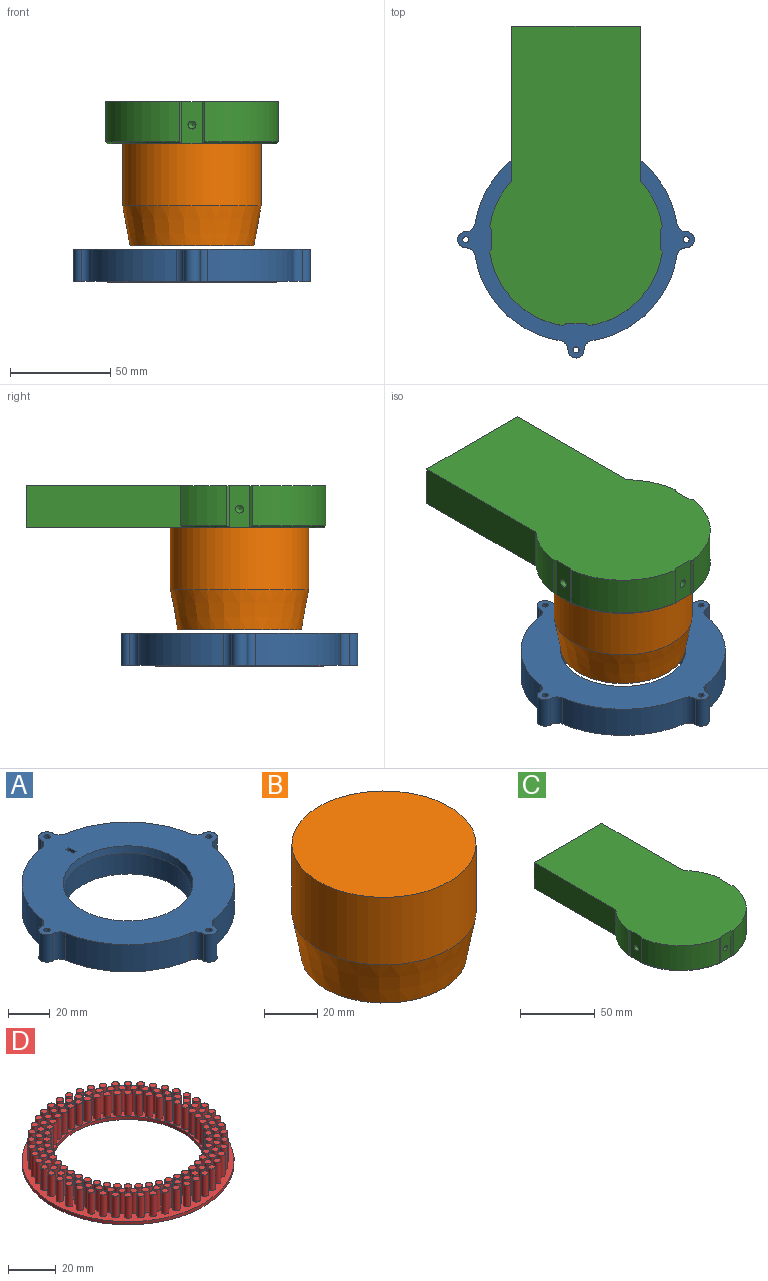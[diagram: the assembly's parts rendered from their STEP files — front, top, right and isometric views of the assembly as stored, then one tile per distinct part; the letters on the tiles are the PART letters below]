
ASSEMBLY  parts=4 mates=3
PART A: 36 faces, bbox 118x118x16 mm
  f0: cylinder r=45mm len=90mm, axis (0,0,1), area 3392.9mm2, adj f5,f22
  f1: cylinder r=1.5mm len=16mm, axis (0,0,-1), area 150.8mm2, adj f5,f35
  f2: cylinder r=1.5mm len=16mm, axis (0,0,-1), area 150.8mm2, adj f5,f35
  f3: cylinder r=1.5mm len=16mm, axis (0,0,-1), area 150.8mm2, adj f5,f35
  f4: cylinder r=1.5mm len=16mm, axis (0,0,-1), area 150.8mm2, adj f5,f35
  f5: plane 118x118mm, normal (0,0,-1), area 2039mm2, adj f0,f1,f2,f3,f4,f6,f7,f8
  f6: cylinder r=4.68mm len=16mm, axis (0,0,-1), area 105.9mm2, adj f5,f8,f20,f35
  f7: cylinder r=4.68mm len=16mm, axis (0,0,-1), area 105.9mm2, adj f5,f8,f21,f35
  f8: cylinder r=4mm len=16mm, axis (0,0,-1), area 201.1mm2, adj f5,f6,f7,f35
  f9: cylinder r=4.68mm len=16mm, axis (0,0,-1), area 105.9mm2, adj f5,f11,f19,f35
  f10: cylinder r=4.68mm len=16mm, axis (0,0,-1), area 105.9mm2, adj f5,f11,f20,f35
  f11: cylinder r=4mm len=16mm, axis (0,0,-1), area 201.1mm2, adj f5,f9,f10,f35
  f12: cylinder r=4.68mm len=16mm, axis (0,0,-1), area 105.9mm2, adj f5,f14,f18,f35
  f13: cylinder r=4.68mm len=16mm, axis (0,0,-1), area 105.9mm2, adj f5,f14,f19,f35
  f14: cylinder r=4mm len=16mm, axis (0,0,-1), area 201.1mm2, adj f5,f12,f13,f35
  f15: cylinder r=4.68mm len=16mm, axis (0,0,-1), area 105.9mm2, adj f5,f16,f18,f35
  f16: cylinder r=4mm len=16mm, axis (0,0,-1), area 201.1mm2, adj f5,f15,f17,f35
  f17: cylinder r=4.68mm len=16mm, axis (0,0,-1), area 105.9mm2, adj f5,f16,f21,f35
  f18: cylinder r=51mm len=42.43mm, axis (0,0,1), area 1026.3mm2, adj f5,f12,f15,f35
  f19: cylinder r=51mm len=42.43mm, axis (0,0,1), area 1026.3mm2, adj f5,f9,f13,f35
  f20: cylinder r=51mm len=42.43mm, axis (0,0,1), area 1026.3mm2, adj f5,f6,f10,f35
  f21: cylinder r=51mm len=42.43mm, axis (0,0,1), area 1026.3mm2, adj f5,f7,f17,f35
  f22: plane 90x90mm, normal (0,0,-1), area 279.6mm2, adj f0,f24
  f23: plane 67x67mm, normal (0,0,-1), area 408.4mm2, adj f25,f31
  f24: cylinder r=44mm len=88mm, axis (0,0,-1), area 552.9mm2, adj f22,f26
  f25: cylinder r=33.5mm len=67mm, axis (0,0,-1), area 421mm2, adj f23,f26
  f26: plane 88x88mm, normal (0,0,-1), area 2546.5mm2, adj f24,f25,f27,f28,f29,f30
  f27: plane 5x2mm, normal (1,0,0), area 10mm2, adj f26,f28,f30,f35
  f28: plane 2x2mm, normal (0,1,0), area 4mm2, adj f26,f27,f29,f35
  f29: plane 5x2mm, normal (-1,0,0), area 10mm2, adj f26,f28,f30,f35
  f30: plane 2x2mm, normal (0,-1,0), area 4mm2, adj f26,f27,f29,f35
  f31: cylinder r=31.5mm len=63mm, axis (0,0,1), area 2375mm2, adj f23,f32
  f32: plane 63x63mm, normal (0,0,-1), area 194.8mm2, adj f31,f33
  f33: cylinder r=30.5mm len=61mm, axis (0,0,1), area 2299.6mm2, adj f32,f34
  f34: cone r=31.92mm half-angle=10.2deg, axis (0,0,1), area 788.1mm2, adj f33,f35
  f35: plane 118x118mm, normal (0,0,1), area 5328.6mm2, adj f1,f2,f3,f4,f6,f7,f8,f9
PART B: 4 faces, bbox 69x69x51 mm
  f0: cylinder r=34.5mm len=69mm, axis (0,0,1), area 6719.9mm2, adj f1,f3
  f1: plane 69x69mm, normal (0,0,1), area 3739.3mm2, adj f0
  f2: plane 61.8x61.8mm, normal (0,0,-1), area 2999.6mm2, adj f3
  f3: cone r=34.5mm half-angle=10.2deg, axis (0,0,1), area 4175.2mm2, adj f0,f2
PART C: 28 faces, bbox 86.4x149.7x21 mm
  f0: plane 21.02x1.32mm, normal (-0.83,0.56,0), area 32.3mm2, adj f1,f15,f16,f17,f27
  f1: cylinder r=43.5mm len=36.68mm, axis (0,0,-1), area 1111.7mm2, adj f0,f2,f16,f27
  f2: plane 21.02x1.32mm, normal (0.56,-0.83,0), area 32.3mm2, adj f1,f3,f16,f17,f27
  f3: plane 21x10.1mm, normal (0,-1,0), area 199.5mm2, adj f2,f4,f16,f17,f23
  f4: plane 21.02x1.32mm, normal (-0.56,-0.83,0), area 32.3mm2, adj f3,f5,f16,f17,f26
  f5: cylinder r=43.5mm len=36.68mm, axis (0,0,-1), area 1111.7mm2, adj f4,f6,f16,f26
  f6: plane 21.02x1.32mm, normal (0.83,0.56,0), area 32.3mm2, adj f5,f7,f16,f17,f26
  f7: plane 21x10.1mm, normal (1,0,0), area 199.5mm2, adj f6,f8,f16,f17,f21
  f8: plane 21.02x1.32mm, normal (0.83,-0.56,0), area 32.3mm2, adj f7,f9,f16,f17,f24
  f9: cylinder r=43.5mm len=23.12mm, axis (0,0,-1), area 520mm2, adj f8,f10,f16,f24
  f10: plane 78.51x21.02mm, normal (1,0,0), area 1617.7mm2, adj f9,f11,f16,f17,f24
  f11: plane 64x21mm, normal (0,1,0), area 1344mm2, adj f10,f12,f16,f17
  f12: plane 78.51x21.02mm, normal (-1,0,0), area 1617.7mm2, adj f11,f13,f16,f17,f25
  f13: cylinder r=43.5mm len=23.12mm, axis (0,0,-1), area 520mm2, adj f12,f14,f16,f25
  f14: plane 21.02x1.32mm, normal (-0.83,-0.56,0), area 32.3mm2, adj f13,f15,f16,f17,f25
  f15: plane 21x10.1mm, normal (-1,0,0), area 199.5mm2, adj f0,f14,f16,f17,f19
  f16: plane 149.5x86.07mm, normal (0,0,1), area 10209.4mm2, adj f0,f1,f2,f3,f4,f5,f6,f7
  f17: plane 148.66x84.38mm, normal (0,0,-1), area 10045.9mm2, adj f0,f2,f3,f4,f6,f7,f8,f10
  f18: cone r=0mm half-angle=59deg, axis (-1,0,0), area 14.7mm2, adj f19
  f19: cylinder r=2mm len=5mm, axis (-1,0,0), area 62.8mm2, adj f15,f18
  f20: cone r=0mm half-angle=59deg, axis (1,0,0), area 14.7mm2, adj f21
  f21: cylinder r=2mm len=5mm, axis (1,0,0), area 62.8mm2, adj f7,f20
  f22: cone r=0mm half-angle=59deg, axis (0,-1,0), area 14.7mm2, adj f23
  f23: cylinder r=2mm len=5mm, axis (0,-1,0), area 62.8mm2, adj f3,f22
  f24: cone r=43.5mm half-angle=45deg, axis (0,0,1), area 36.3mm2, adj f8,f9,f10,f17
  f25: cone r=43.5mm half-angle=45deg, axis (0,0,1), area 36.3mm2, adj f12,f13,f14,f17
  f26: cone r=43.5mm half-angle=45deg, axis (0,0,1), area 79.3mm2, adj f4,f5,f6,f17
  f27: cone r=43.5mm half-angle=45deg, axis (0,0,1), area 79.3mm2, adj f0,f1,f2,f17
PART D: 292 faces, bbox 89x89x12.6 mm
  f0: cylinder r=32mm len=64mm, axis (0,0,-1), area 321.7mm2, adj f2,f3
  f1: cylinder r=44.5mm len=89mm, axis (0,0,-1), area 447.4mm2, adj f2,f3
  f2: plane 89x89mm, normal (0,0,1), area 1917.3mm2, adj f0,f1,f4,f6,f8,f10,f12,f14
  f3: plane 89x89mm, normal (0,0,-1), area 3004.1mm2, adj f0,f1
  f4: cylinder r=1.55mm len=11mm, axis (0,0,-1), area 107.1mm2, adj f2,f5
  f5: plane 3.1x3.1mm, normal (0,0,1), area 7.5mm2, adj f4
  f6: cylinder r=1.55mm len=11mm, axis (0,0,-1), area 107.1mm2, adj f2,f7
  f7: plane 3.1x3.1mm, normal (0,0,1), area 7.5mm2, adj f6
  f8: cylinder r=1.55mm len=11mm, axis (0,0,-1), area 107.1mm2, adj f2,f9
  f9: plane 3.1x3.1mm, normal (0,0,1), area 7.5mm2, adj f8
  f10: cylinder r=1.55mm len=11mm, axis (0,0,-1), area 107.1mm2, adj f2,f11
  f11: plane 3.1x3.1mm, normal (0,0,1), area 7.5mm2, adj f10
  f12: cylinder r=1.55mm len=11mm, axis (0,0,-1), area 107.1mm2, adj f2,f13
  f13: plane 3.1x3.1mm, normal (0,0,1), area 7.5mm2, adj f12
  f14: cylinder r=1.55mm len=11mm, axis (0,0,-1), area 107.1mm2, adj f2,f15
  f15: plane 3.1x3.1mm, normal (0,0,1), area 7.5mm2, adj f14
  f16: cylinder r=1.55mm len=11mm, axis (0,0,-1), area 107.1mm2, adj f2,f17
  f17: plane 3.1x3.1mm, normal (0,0,1), area 7.5mm2, adj f16
  f18: cylinder r=1.55mm len=11mm, axis (0,0,-1), area 107.1mm2, adj f2,f19
  f19: plane 3.1x3.1mm, normal (0,0,1), area 7.5mm2, adj f18
  f20: cylinder r=1.55mm len=11mm, axis (0,0,-1), area 107.1mm2, adj f2,f21
  f21: plane 3.1x3.1mm, normal (0,0,1), area 7.5mm2, adj f20
  f22: cylinder r=1.55mm len=11mm, axis (0,0,-1), area 107.1mm2, adj f2,f23
  f23: plane 3.1x3.1mm, normal (0,0,1), area 7.5mm2, adj f22
  f24: cylinder r=1.55mm len=11mm, axis (0,0,-1), area 107.1mm2, adj f2,f25
  f25: plane 3.1x3.1mm, normal (0,0,1), area 7.5mm2, adj f24
  f26: cylinder r=1.55mm len=11mm, axis (0,0,-1), area 107.1mm2, adj f2,f27
  f27: plane 3.1x3.1mm, normal (0,0,1), area 7.5mm2, adj f26
  f28: cylinder r=1.55mm len=11mm, axis (0,0,-1), area 107.1mm2, adj f2,f29
  f29: plane 3.1x3.1mm, normal (0,0,1), area 7.5mm2, adj f28
  f30: cylinder r=1.55mm len=11mm, axis (0,0,-1), area 107.1mm2, adj f2,f31
  f31: plane 3.1x3.1mm, normal (0,0,1), area 7.5mm2, adj f30
  f32: cylinder r=1.55mm len=11mm, axis (0,0,-1), area 107.1mm2, adj f2,f33
  f33: plane 3.1x3.1mm, normal (0,0,1), area 7.5mm2, adj f32
  f34: cylinder r=1.55mm len=11mm, axis (0,0,-1), area 107.1mm2, adj f2,f35
  f35: plane 3.1x3.1mm, normal (0,0,1), area 7.5mm2, adj f34
  f36: cylinder r=1.55mm len=11mm, axis (0,0,-1), area 107.1mm2, adj f2,f37
  f37: plane 3.1x3.1mm, normal (0,0,1), area 7.5mm2, adj f36
  f38: cylinder r=1.55mm len=11mm, axis (0,0,-1), area 107.1mm2, adj f2,f39
  f39: plane 3.1x3.1mm, normal (0,0,1), area 7.5mm2, adj f38
  f40: cylinder r=1.55mm len=11mm, axis (0,0,-1), area 107.1mm2, adj f2,f41
  f41: plane 3.1x3.1mm, normal (0,0,1), area 7.5mm2, adj f40
  f42: cylinder r=1.55mm len=11mm, axis (0,0,-1), area 107.1mm2, adj f2,f43
  f43: plane 3.1x3.1mm, normal (0,0,1), area 7.5mm2, adj f42
  f44: cylinder r=1.55mm len=11mm, axis (0,0,-1), area 107.1mm2, adj f2,f45
  f45: plane 3.1x3.1mm, normal (0,0,1), area 7.5mm2, adj f44
  f46: cylinder r=1.55mm len=11mm, axis (0,0,-1), area 107.1mm2, adj f2,f47
  f47: plane 3.1x3.1mm, normal (0,0,1), area 7.5mm2, adj f46
  f48: cylinder r=1.55mm len=11mm, axis (0,0,-1), area 107.1mm2, adj f2,f49
  f49: plane 3.1x3.1mm, normal (0,0,1), area 7.5mm2, adj f48
  f50: cylinder r=1.55mm len=11mm, axis (0,0,-1), area 107.1mm2, adj f2,f51
  f51: plane 3.1x3.1mm, normal (0,0,1), area 7.5mm2, adj f50
  f52: cylinder r=1.55mm len=11mm, axis (0,0,-1), area 107.1mm2, adj f2,f53
  f53: plane 3.1x3.1mm, normal (0,0,1), area 7.5mm2, adj f52
  f54: cylinder r=1.55mm len=11mm, axis (0,0,-1), area 107.1mm2, adj f2,f55
  f55: plane 3.1x3.1mm, normal (0,0,1), area 7.5mm2, adj f54
  f56: cylinder r=1.55mm len=11mm, axis (0,0,-1), area 107.1mm2, adj f2,f57
  f57: plane 3.1x3.1mm, normal (0,0,1), area 7.5mm2, adj f56
  f58: cylinder r=1.55mm len=11mm, axis (0,0,-1), area 107.1mm2, adj f2,f59
  f59: plane 3.1x3.1mm, normal (0,0,1), area 7.5mm2, adj f58
  f60: cylinder r=1.55mm len=11mm, axis (0,0,-1), area 107.1mm2, adj f2,f61
  f61: plane 3.1x3.1mm, normal (0,0,1), area 7.5mm2, adj f60
  f62: cylinder r=1.55mm len=11mm, axis (0,0,-1), area 107.1mm2, adj f2,f63
  f63: plane 3.1x3.1mm, normal (0,0,1), area 7.5mm2, adj f62
  f64: cylinder r=1.55mm len=11mm, axis (0,0,-1), area 107.1mm2, adj f2,f65
  f65: plane 3.1x3.1mm, normal (0,0,1), area 7.5mm2, adj f64
  f66: cylinder r=1.55mm len=11mm, axis (0,0,-1), area 107.1mm2, adj f2,f67
  f67: plane 3.1x3.1mm, normal (0,0,1), area 7.5mm2, adj f66
  f68: cylinder r=1.55mm len=11mm, axis (0,0,-1), area 107.1mm2, adj f2,f69
  f69: plane 3.1x3.1mm, normal (0,0,1), area 7.5mm2, adj f68
  f70: cylinder r=1.55mm len=11mm, axis (0,0,-1), area 107.1mm2, adj f2,f71
  f71: plane 3.1x3.1mm, normal (0,0,1), area 7.5mm2, adj f70
  f72: cylinder r=1.55mm len=11mm, axis (0,0,-1), area 107.1mm2, adj f2,f73
  f73: plane 3.1x3.1mm, normal (0,0,1), area 7.5mm2, adj f72
  f74: cylinder r=1.55mm len=11mm, axis (0,0,-1), area 107.1mm2, adj f2,f75
  f75: plane 3.1x3.1mm, normal (0,0,1), area 7.5mm2, adj f74
  f76: cylinder r=1.55mm len=11mm, axis (0,0,-1), area 107.1mm2, adj f2,f77
  f77: plane 3.1x3.1mm, normal (0,0,1), area 7.5mm2, adj f76
  f78: cylinder r=1.55mm len=11mm, axis (0,0,-1), area 107.1mm2, adj f2,f79
  f79: plane 3.1x3.1mm, normal (0,0,1), area 7.5mm2, adj f78
  f80: cylinder r=1.55mm len=11mm, axis (0,0,-1), area 107.1mm2, adj f2,f81
  f81: plane 3.1x3.1mm, normal (0,0,1), area 7.5mm2, adj f80
  f82: cylinder r=1.55mm len=11mm, axis (0,0,-1), area 107.1mm2, adj f2,f83
  f83: plane 3.1x3.1mm, normal (0,0,1), area 7.5mm2, adj f82
  f84: cylinder r=1.55mm len=11mm, axis (0,0,-1), area 107.1mm2, adj f2,f85
  f85: plane 3.1x3.1mm, normal (0,0,1), area 7.5mm2, adj f84
  f86: cylinder r=1.55mm len=11mm, axis (0,0,-1), area 107.1mm2, adj f2,f87
  f87: plane 3.1x3.1mm, normal (0,0,1), area 7.5mm2, adj f86
  f88: cylinder r=1.55mm len=11mm, axis (0,0,-1), area 107.1mm2, adj f2,f89
  f89: plane 3.1x3.1mm, normal (0,0,1), area 7.5mm2, adj f88
  f90: cylinder r=1.55mm len=11mm, axis (0,0,-1), area 107.1mm2, adj f2,f91
  f91: plane 3.1x3.1mm, normal (0,0,1), area 7.5mm2, adj f90
  f92: cylinder r=1.55mm len=11mm, axis (0,0,-1), area 107.1mm2, adj f2,f93
  f93: plane 3.1x3.1mm, normal (0,0,1), area 7.5mm2, adj f92
  f94: cylinder r=1.55mm len=11mm, axis (0,0,-1), area 107.1mm2, adj f2,f95
  f95: plane 3.1x3.1mm, normal (0,0,1), area 7.5mm2, adj f94
  f96: cylinder r=1.55mm len=11mm, axis (0,0,-1), area 107.1mm2, adj f2,f97
  f97: plane 3.1x3.1mm, normal (0,0,1), area 7.5mm2, adj f96
  f98: cylinder r=1.55mm len=11mm, axis (0,0,-1), area 107.1mm2, adj f2,f99
  f99: plane 3.1x3.1mm, normal (0,0,1), area 7.5mm2, adj f98
  f100: cylinder r=1.55mm len=11mm, axis (0,0,-1), area 107.1mm2, adj f2,f101
  f101: plane 3.1x3.1mm, normal (0,0,1), area 7.5mm2, adj f100
  f102: cylinder r=1.55mm len=11mm, axis (0,0,-1), area 107.1mm2, adj f2,f103
  f103: plane 3.1x3.1mm, normal (0,0,1), area 7.5mm2, adj f102
  f104: cylinder r=1.55mm len=11mm, axis (0,0,-1), area 107.1mm2, adj f2,f105
  f105: plane 3.1x3.1mm, normal (0,0,1), area 7.5mm2, adj f104
  f106: cylinder r=1.55mm len=11mm, axis (0,0,-1), area 107.1mm2, adj f2,f107
  f107: plane 3.1x3.1mm, normal (0,0,1), area 7.5mm2, adj f106
  f108: cylinder r=1.55mm len=11mm, axis (0,0,-1), area 107.1mm2, adj f2,f109
  f109: plane 3.1x3.1mm, normal (0,0,1), area 7.5mm2, adj f108
  f110: cylinder r=1.55mm len=11mm, axis (0,0,-1), area 107.1mm2, adj f2,f111
  f111: plane 3.1x3.1mm, normal (0,0,1), area 7.5mm2, adj f110
  f112: cylinder r=1.55mm len=11mm, axis (0,0,-1), area 107.1mm2, adj f2,f113
  f113: plane 3.1x3.1mm, normal (0,0,1), area 7.5mm2, adj f112
  f114: cylinder r=1.55mm len=11mm, axis (0,0,-1), area 107.1mm2, adj f2,f115
  f115: plane 3.1x3.1mm, normal (0,0,1), area 7.5mm2, adj f114
  f116: cylinder r=1.55mm len=11mm, axis (0,0,-1), area 107.1mm2, adj f2,f117
  f117: plane 3.1x3.1mm, normal (0,0,1), area 7.5mm2, adj f116
  f118: cylinder r=1.55mm len=11mm, axis (0,0,-1), area 107.1mm2, adj f2,f119
  f119: plane 3.1x3.1mm, normal (0,0,1), area 7.5mm2, adj f118
  f120: cylinder r=1.55mm len=11mm, axis (0,0,-1), area 107.1mm2, adj f2,f121
  f121: plane 3.1x3.1mm, normal (0,0,1), area 7.5mm2, adj f120
  f122: cylinder r=1.55mm len=11mm, axis (0,0,-1), area 107.1mm2, adj f2,f123
  f123: plane 3.1x3.1mm, normal (0,0,1), area 7.5mm2, adj f122
  f124: cylinder r=1.55mm len=11mm, axis (0,0,-1), area 107.1mm2, adj f2,f125
  f125: plane 3.1x3.1mm, normal (0,0,1), area 7.5mm2, adj f124
  f126: cylinder r=1.55mm len=11mm, axis (0,0,-1), area 107.1mm2, adj f2,f127
  f127: plane 3.1x3.1mm, normal (0,0,1), area 7.5mm2, adj f126
  f128: cylinder r=1.55mm len=11mm, axis (0,0,-1), area 107.1mm2, adj f2,f129
  f129: plane 3.1x3.1mm, normal (0,0,1), area 7.5mm2, adj f128
  f130: cylinder r=1.55mm len=11mm, axis (0,0,-1), area 107.1mm2, adj f2,f131
  f131: plane 3.1x3.1mm, normal (0,0,1), area 7.5mm2, adj f130
  f132: cylinder r=1.55mm len=11mm, axis (0,0,-1), area 107.1mm2, adj f2,f133
  f133: plane 3.1x3.1mm, normal (0,0,1), area 7.5mm2, adj f132
  f134: cylinder r=1.55mm len=11mm, axis (0,0,-1), area 107.1mm2, adj f2,f135
  f135: plane 3.1x3.1mm, normal (0,0,1), area 7.5mm2, adj f134
  f136: cylinder r=1.55mm len=11mm, axis (0,0,-1), area 107.1mm2, adj f2,f137
  f137: plane 3.1x3.1mm, normal (0,0,1), area 7.5mm2, adj f136
  f138: cylinder r=1.55mm len=11mm, axis (0,0,-1), area 107.1mm2, adj f2,f139
  f139: plane 3.1x3.1mm, normal (0,0,1), area 7.5mm2, adj f138
  f140: cylinder r=1.55mm len=11mm, axis (0,0,-1), area 107.1mm2, adj f2,f141
  f141: plane 3.1x3.1mm, normal (0,0,1), area 7.5mm2, adj f140
  f142: cylinder r=1.55mm len=11mm, axis (0,0,-1), area 107.1mm2, adj f2,f143
  f143: plane 3.1x3.1mm, normal (0,0,1), area 7.5mm2, adj f142
  f144: cylinder r=1.55mm len=11mm, axis (0,0,-1), area 107.1mm2, adj f2,f145
  f145: plane 3.1x3.1mm, normal (0,0,1), area 7.5mm2, adj f144
  f146: cylinder r=1.55mm len=11mm, axis (0,0,-1), area 107.1mm2, adj f2,f147
  f147: plane 3.1x3.1mm, normal (0,0,1), area 7.5mm2, adj f146
  f148: cylinder r=1.55mm len=11mm, axis (0,0,-1), area 107.1mm2, adj f2,f149
  f149: plane 3.1x3.1mm, normal (0,0,1), area 7.5mm2, adj f148
  f150: cylinder r=1.55mm len=11mm, axis (0,0,-1), area 107.1mm2, adj f2,f151
  f151: plane 3.1x3.1mm, normal (0,0,1), area 7.5mm2, adj f150
  f152: cylinder r=1.55mm len=11mm, axis (0,0,-1), area 107.1mm2, adj f2,f153
  f153: plane 3.1x3.1mm, normal (0,0,1), area 7.5mm2, adj f152
  f154: cylinder r=1.55mm len=11mm, axis (0,0,-1), area 107.1mm2, adj f2,f155
  f155: plane 3.1x3.1mm, normal (0,0,1), area 7.5mm2, adj f154
  f156: cylinder r=1.55mm len=11mm, axis (0,0,-1), area 107.1mm2, adj f2,f157
  f157: plane 3.1x3.1mm, normal (0,0,1), area 7.5mm2, adj f156
  f158: cylinder r=1.55mm len=11mm, axis (0,0,-1), area 107.1mm2, adj f2,f159
  f159: plane 3.1x3.1mm, normal (0,0,1), area 7.5mm2, adj f158
  f160: cylinder r=1.55mm len=11mm, axis (0,0,-1), area 107.1mm2, adj f2,f161
  f161: plane 3.1x3.1mm, normal (0,0,1), area 7.5mm2, adj f160
  f162: cylinder r=1.55mm len=11mm, axis (0,0,-1), area 107.1mm2, adj f2,f163
  f163: plane 3.1x3.1mm, normal (0,0,1), area 7.5mm2, adj f162
  f164: cylinder r=1.55mm len=11mm, axis (0,0,-1), area 107.1mm2, adj f2,f165
  f165: plane 3.1x3.1mm, normal (0,0,1), area 7.5mm2, adj f164
  f166: cylinder r=1.55mm len=11mm, axis (0,0,-1), area 107.1mm2, adj f2,f167
  f167: plane 3.1x3.1mm, normal (0,0,1), area 7.5mm2, adj f166
  f168: cylinder r=1.55mm len=11mm, axis (0,0,-1), area 107.1mm2, adj f2,f169
  f169: plane 3.1x3.1mm, normal (0,0,1), area 7.5mm2, adj f168
  f170: cylinder r=1.55mm len=11mm, axis (0,0,-1), area 107.1mm2, adj f2,f171
  f171: plane 3.1x3.1mm, normal (0,0,1), area 7.5mm2, adj f170
  f172: cylinder r=1.55mm len=11mm, axis (0,0,-1), area 107.1mm2, adj f2,f173
  f173: plane 3.1x3.1mm, normal (0,0,1), area 7.5mm2, adj f172
  f174: cylinder r=1.55mm len=11mm, axis (0,0,-1), area 107.1mm2, adj f2,f175
  f175: plane 3.1x3.1mm, normal (0,0,1), area 7.5mm2, adj f174
  f176: cylinder r=1.55mm len=11mm, axis (0,0,-1), area 107.1mm2, adj f2,f177
  f177: plane 3.1x3.1mm, normal (0,0,1), area 7.5mm2, adj f176
  f178: cylinder r=1.55mm len=11mm, axis (0,0,-1), area 107.1mm2, adj f2,f179
  f179: plane 3.1x3.1mm, normal (0,0,1), area 7.5mm2, adj f178
  f180: cylinder r=1.55mm len=11mm, axis (0,0,-1), area 107.1mm2, adj f2,f181
  f181: plane 3.1x3.1mm, normal (0,0,1), area 7.5mm2, adj f180
  f182: cylinder r=1.55mm len=11mm, axis (0,0,-1), area 107.1mm2, adj f2,f183
  f183: plane 3.1x3.1mm, normal (0,0,1), area 7.5mm2, adj f182
  f184: cylinder r=1.55mm len=11mm, axis (0,0,-1), area 107.1mm2, adj f2,f185
  f185: plane 3.1x3.1mm, normal (0,0,1), area 7.5mm2, adj f184
  f186: cylinder r=1.55mm len=11mm, axis (0,0,-1), area 107.1mm2, adj f2,f187
  f187: plane 3.1x3.1mm, normal (0,0,1), area 7.5mm2, adj f186
  f188: cylinder r=1.55mm len=11mm, axis (0,0,-1), area 107.1mm2, adj f2,f189
  f189: plane 3.1x3.1mm, normal (0,0,1), area 7.5mm2, adj f188
  f190: cylinder r=1.55mm len=11mm, axis (0,0,-1), area 107.1mm2, adj f2,f191
  f191: plane 3.1x3.1mm, normal (0,0,1), area 7.5mm2, adj f190
  f192: cylinder r=1.55mm len=11mm, axis (0,0,-1), area 107.1mm2, adj f2,f193
  f193: plane 3.1x3.1mm, normal (0,0,1), area 7.5mm2, adj f192
  f194: cylinder r=1.55mm len=11mm, axis (0,0,-1), area 107.1mm2, adj f2,f195
  f195: plane 3.1x3.1mm, normal (0,0,1), area 7.5mm2, adj f194
  f196: cylinder r=1.55mm len=11mm, axis (0,0,-1), area 107.1mm2, adj f2,f197
  f197: plane 3.1x3.1mm, normal (0,0,1), area 7.5mm2, adj f196
  f198: cylinder r=1.55mm len=11mm, axis (0,0,-1), area 107.1mm2, adj f2,f199
  f199: plane 3.1x3.1mm, normal (0,0,1), area 7.5mm2, adj f198
  f200: cylinder r=1.55mm len=11mm, axis (0,0,-1), area 107.1mm2, adj f2,f201
  f201: plane 3.1x3.1mm, normal (0,0,1), area 7.5mm2, adj f200
  f202: cylinder r=1.55mm len=11mm, axis (0,0,-1), area 107.1mm2, adj f2,f203
  f203: plane 3.1x3.1mm, normal (0,0,1), area 7.5mm2, adj f202
  f204: cylinder r=1.55mm len=11mm, axis (0,0,-1), area 107.1mm2, adj f2,f205
  f205: plane 3.1x3.1mm, normal (0,0,1), area 7.5mm2, adj f204
  f206: cylinder r=1.55mm len=11mm, axis (0,0,-1), area 107.1mm2, adj f2,f207
  f207: plane 3.1x3.1mm, normal (0,0,1), area 7.5mm2, adj f206
  f208: cylinder r=1.55mm len=11mm, axis (0,0,-1), area 107.1mm2, adj f2,f209
  f209: plane 3.1x3.1mm, normal (0,0,1), area 7.5mm2, adj f208
  f210: cylinder r=1.55mm len=11mm, axis (0,0,-1), area 107.1mm2, adj f2,f211
  f211: plane 3.1x3.1mm, normal (0,0,1), area 7.5mm2, adj f210
  f212: cylinder r=1.55mm len=11mm, axis (0,0,-1), area 107.1mm2, adj f2,f213
  f213: plane 3.1x3.1mm, normal (0,0,1), area 7.5mm2, adj f212
  f214: cylinder r=1.55mm len=11mm, axis (0,0,-1), area 107.1mm2, adj f2,f215
  f215: plane 3.1x3.1mm, normal (0,0,1), area 7.5mm2, adj f214
  f216: cylinder r=1.55mm len=11mm, axis (0,0,-1), area 107.1mm2, adj f2,f217
  f217: plane 3.1x3.1mm, normal (0,0,1), area 7.5mm2, adj f216
  f218: cylinder r=1.55mm len=11mm, axis (0,0,-1), area 107.1mm2, adj f2,f219
  f219: plane 3.1x3.1mm, normal (0,0,1), area 7.5mm2, adj f218
  f220: cylinder r=1.55mm len=11mm, axis (0,0,-1), area 107.1mm2, adj f2,f221
  f221: plane 3.1x3.1mm, normal (0,0,1), area 7.5mm2, adj f220
  f222: cylinder r=1.55mm len=11mm, axis (0,0,-1), area 107.1mm2, adj f2,f223
  f223: plane 3.1x3.1mm, normal (0,0,1), area 7.5mm2, adj f222
  f224: cylinder r=1.55mm len=11mm, axis (0,0,-1), area 107.1mm2, adj f2,f225
  f225: plane 3.1x3.1mm, normal (0,0,1), area 7.5mm2, adj f224
  f226: cylinder r=1.55mm len=11mm, axis (0,0,-1), area 107.1mm2, adj f2,f227
  f227: plane 3.1x3.1mm, normal (0,0,1), area 7.5mm2, adj f226
  f228: cylinder r=1.55mm len=11mm, axis (0,0,-1), area 107.1mm2, adj f2,f229
  f229: plane 3.1x3.1mm, normal (0,0,1), area 7.5mm2, adj f228
  f230: cylinder r=1.55mm len=11mm, axis (0,0,-1), area 107.1mm2, adj f2,f231
  f231: plane 3.1x3.1mm, normal (0,0,1), area 7.5mm2, adj f230
  f232: cylinder r=1.55mm len=11mm, axis (0,0,-1), area 107.1mm2, adj f2,f233
  f233: plane 3.1x3.1mm, normal (0,0,1), area 7.5mm2, adj f232
  f234: cylinder r=1.55mm len=11mm, axis (0,0,-1), area 107.1mm2, adj f2,f235
  f235: plane 3.1x3.1mm, normal (0,0,1), area 7.5mm2, adj f234
  f236: cylinder r=1.55mm len=11mm, axis (0,0,-1), area 107.1mm2, adj f2,f237
  f237: plane 3.1x3.1mm, normal (0,0,1), area 7.5mm2, adj f236
  f238: cylinder r=1.55mm len=11mm, axis (0,0,-1), area 107.1mm2, adj f2,f239
  f239: plane 3.1x3.1mm, normal (0,0,1), area 7.5mm2, adj f238
  f240: cylinder r=1.55mm len=11mm, axis (0,0,-1), area 107.1mm2, adj f2,f241
  f241: plane 3.1x3.1mm, normal (0,0,1), area 7.5mm2, adj f240
  f242: cylinder r=1.55mm len=11mm, axis (0,0,-1), area 107.1mm2, adj f2,f243
  f243: plane 3.1x3.1mm, normal (0,0,1), area 7.5mm2, adj f242
  f244: cylinder r=1.55mm len=11mm, axis (0,0,-1), area 107.1mm2, adj f2,f245
  f245: plane 3.1x3.1mm, normal (0,0,1), area 7.5mm2, adj f244
  f246: cylinder r=1.55mm len=11mm, axis (0,0,-1), area 107.1mm2, adj f2,f247
  f247: plane 3.1x3.1mm, normal (0,0,1), area 7.5mm2, adj f246
  f248: cylinder r=1.55mm len=11mm, axis (0,0,-1), area 107.1mm2, adj f2,f249
  f249: plane 3.1x3.1mm, normal (0,0,1), area 7.5mm2, adj f248
  f250: cylinder r=1.55mm len=11mm, axis (0,0,-1), area 107.1mm2, adj f2,f251
  f251: plane 3.1x3.1mm, normal (0,0,1), area 7.5mm2, adj f250
  f252: cylinder r=1.55mm len=11mm, axis (0,0,-1), area 107.1mm2, adj f2,f253
  f253: plane 3.1x3.1mm, normal (0,0,1), area 7.5mm2, adj f252
  f254: cylinder r=1.55mm len=11mm, axis (0,0,-1), area 107.1mm2, adj f2,f255
  f255: plane 3.1x3.1mm, normal (0,0,1), area 7.5mm2, adj f254
  f256: cylinder r=1.55mm len=11mm, axis (0,0,-1), area 107.1mm2, adj f2,f257
  f257: plane 3.1x3.1mm, normal (0,0,1), area 7.5mm2, adj f256
  f258: cylinder r=1.55mm len=11mm, axis (0,0,-1), area 107.1mm2, adj f2,f259
  f259: plane 3.1x3.1mm, normal (0,0,1), area 7.5mm2, adj f258
  f260: cylinder r=1.55mm len=11mm, axis (0,0,-1), area 107.1mm2, adj f2,f261
  f261: plane 3.1x3.1mm, normal (0,0,1), area 7.5mm2, adj f260
  f262: cylinder r=1.55mm len=11mm, axis (0,0,-1), area 107.1mm2, adj f2,f263
  f263: plane 3.1x3.1mm, normal (0,0,1), area 7.5mm2, adj f262
  f264: cylinder r=1.55mm len=11mm, axis (0,0,-1), area 107.1mm2, adj f2,f265
  f265: plane 3.1x3.1mm, normal (0,0,1), area 7.5mm2, adj f264
  f266: cylinder r=1.55mm len=11mm, axis (0,0,-1), area 107.1mm2, adj f2,f267
  f267: plane 3.1x3.1mm, normal (0,0,1), area 7.5mm2, adj f266
  f268: cylinder r=1.55mm len=11mm, axis (0,0,-1), area 107.1mm2, adj f2,f269
  f269: plane 3.1x3.1mm, normal (0,0,1), area 7.5mm2, adj f268
  f270: cylinder r=1.55mm len=11mm, axis (0,0,-1), area 107.1mm2, adj f2,f271
  f271: plane 3.1x3.1mm, normal (0,0,1), area 7.5mm2, adj f270
  f272: cylinder r=1.55mm len=11mm, axis (0,0,-1), area 107.1mm2, adj f2,f273
  f273: plane 3.1x3.1mm, normal (0,0,1), area 7.5mm2, adj f272
  f274: cylinder r=1.55mm len=11mm, axis (0,0,-1), area 107.1mm2, adj f2,f275
  f275: plane 3.1x3.1mm, normal (0,0,1), area 7.5mm2, adj f274
  f276: cylinder r=1.55mm len=11mm, axis (0,0,-1), area 107.1mm2, adj f2,f277
  f277: plane 3.1x3.1mm, normal (0,0,1), area 7.5mm2, adj f276
  f278: cylinder r=1.55mm len=11mm, axis (0,0,-1), area 107.1mm2, adj f2,f279
  f279: plane 3.1x3.1mm, normal (0,0,1), area 7.5mm2, adj f278
  f280: cylinder r=1.55mm len=11mm, axis (0,0,-1), area 107.1mm2, adj f2,f281
  f281: plane 3.1x3.1mm, normal (0,0,1), area 7.5mm2, adj f280
  f282: cylinder r=1.55mm len=11mm, axis (0,0,-1), area 107.1mm2, adj f2,f283
  f283: plane 3.1x3.1mm, normal (0,0,1), area 7.5mm2, adj f282
  f284: cylinder r=1.55mm len=11mm, axis (0,0,-1), area 107.1mm2, adj f2,f285
  f285: plane 3.1x3.1mm, normal (0,0,1), area 7.5mm2, adj f284
  f286: cylinder r=1.55mm len=11mm, axis (0,0,-1), area 107.1mm2, adj f2,f287
  f287: plane 3.1x3.1mm, normal (0,0,1), area 7.5mm2, adj f286
  f288: cylinder r=1.55mm len=11mm, axis (0,0,-1), area 107.1mm2, adj f2,f289
  f289: plane 3.1x3.1mm, normal (0,0,1), area 7.5mm2, adj f288
  f290: cylinder r=1.55mm len=11mm, axis (0,0,-1), area 107.1mm2, adj f2,f291
  f291: plane 3.1x3.1mm, normal (0,0,1), area 7.5mm2, adj f290
PLACE A t=(3.91,-4.17,2.33)mm
PLACE B t=(3.91,-4.17,0)mm
PLACE C t=(3.91,-4.17,0)mm
PLACE D rot(axis=(0,1,0),180deg) t=(3.91,-4.17,-56.53)mm
MATE fastened D.f1 <-> A.f0  axis (0,0,1) through (3.91,-4.17,-56.53)mm
MATE cylindrical B.f0 <-> D.f1  axis (0,0,-1) through (3.91,-4.17,-51)mm
MATE fastened B.f0 <-> C.f13  axis (0,0,1) through (3.91,-4.17,0)mm
